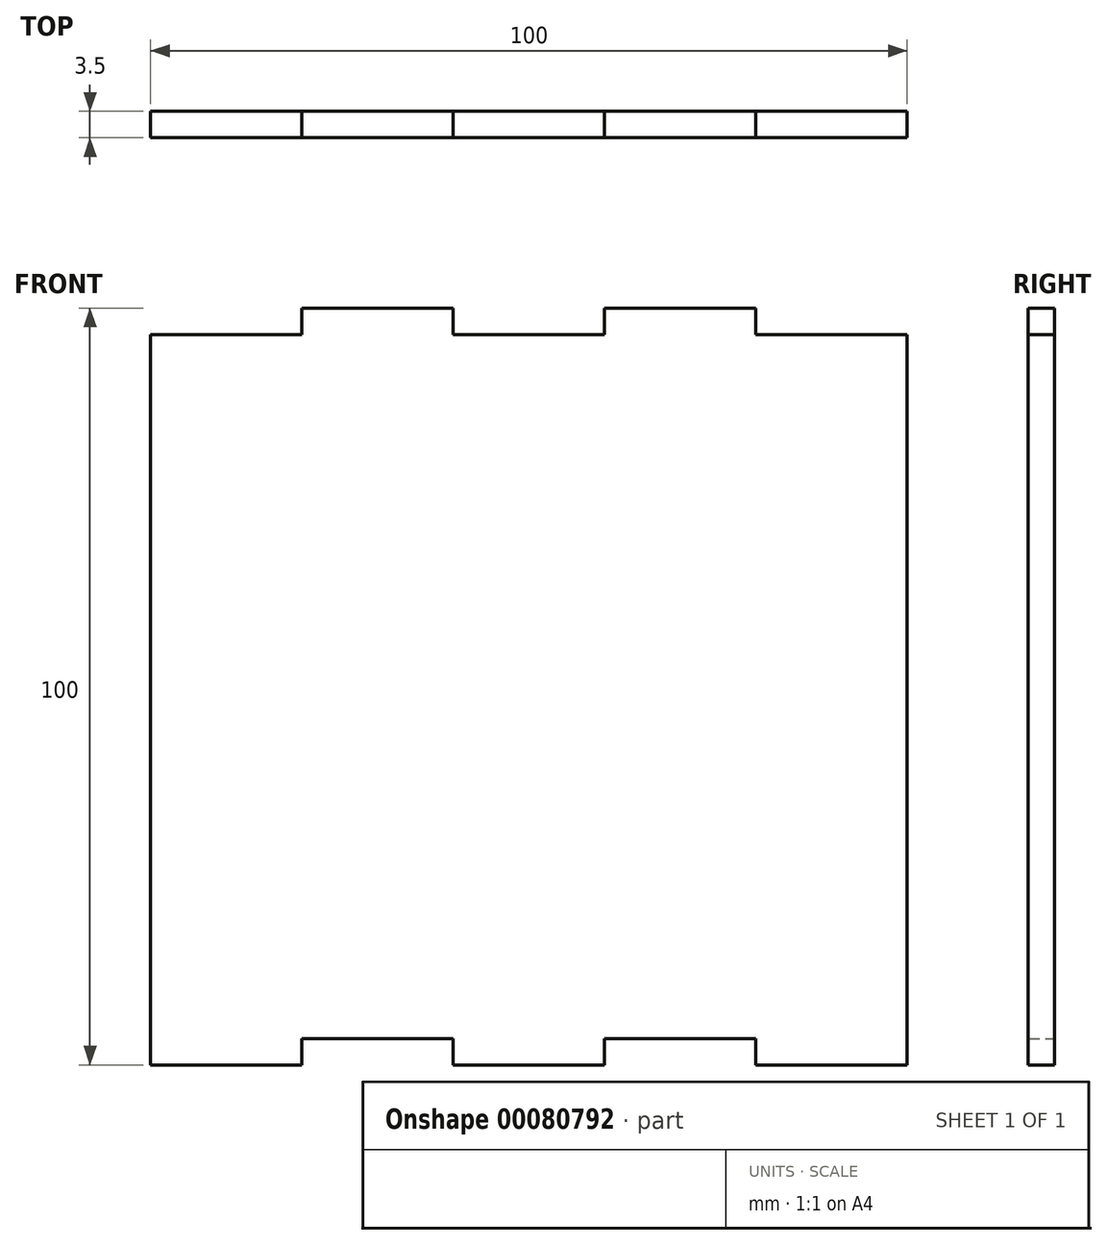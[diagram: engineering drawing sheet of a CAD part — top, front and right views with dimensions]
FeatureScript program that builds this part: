
annotation { "Feature Type Name" : "Feature", "Feature Type Description" : "" }
export const myFeature = defineFeature(function(context is Context, id is Id, definition is map)
    precondition{}
    {
        {
            var Q0;
            Q0=qCreatedBy(makeId("Front.planeOp"),FACE);
            var sketch = newSketch(context, id + "F0", { "sketchPlane" : qUnion([Q0])});
            skLineSegment(sketch, "E0.bottom", {"start": v(-60, 1.92) * mm, "end": v(40, 1.92) * mm});
            skLineSegment(sketch, "E0.top", {"start": v(-60, -98.08) * mm, "end": v(40, -98.08) * mm});
            skLineSegment(sketch, "E0.left", {"start": v(-60, 1.92) * mm, "end": v(-60, -98.08) * mm});
            skLineSegment(sketch, "E0.right", {"start": v(40, 1.92) * mm, "end": v(40, -98.08) * mm});
            skLineSegment(sketch, "E1.direction1", {"start": v(-60, -98.08) * mm, "end": v(-49.65, -98.08) * mm, "construction": true});
            skLineSegment(sketch, "E2", {"start": v(-40, -98.08) * mm, "end": v(-40, -94.58) * mm});
            skLineSegment(sketch, "E3", {"start": v(-40, -94.58) * mm, "end": v(-20, -94.58) * mm});
            skLineSegment(sketch, "E4", {"start": v(-20, -94.58) * mm, "end": v(-20, -98.08) * mm});
            skLineSegment(sketch, "E5", {"start": v(-20, -98.08) * mm, "end": v(0, -98.08) * mm});
            skLineSegment(sketch, "E6", {"start": v(0, -98.08) * mm, "end": v(0, -94.58) * mm});
            skLineSegment(sketch, "E7", {"start": v(-60, -98.08) * mm, "end": v(-40, -98.08) * mm});
            skLineSegment(sketch, "E8", {"start": v(0, -94.58) * mm, "end": v(20, -94.58) * mm});
            skLineSegment(sketch, "E9", {"start": v(20, -94.58) * mm, "end": v(20, -98.08) * mm});
            skLineSegment(sketch, "E10", {"start": v(-60, -1.58) * mm, "end": v(-40, -1.58) * mm});
            skLineSegment(sketch, "E11", {"start": v(-40, -1.58) * mm, "end": v(-40, 1.92) * mm});
            skLineSegment(sketch, "E12", {"start": v(-40, 1.92) * mm, "end": v(-20, 1.92) * mm});
            skLineSegment(sketch, "E13", {"start": v(-20, 1.92) * mm, "end": v(-20, -1.58) * mm});
            skLineSegment(sketch, "E14", {"start": v(-20, -1.58) * mm, "end": v(0, -1.58) * mm});
            skLineSegment(sketch, "E15", {"start": v(0, -1.58) * mm, "end": v(0, 1.92) * mm});
            skLineSegment(sketch, "E16", {"start": v(0, 1.92) * mm, "end": v(20, 1.92) * mm});
            skLineSegment(sketch, "E17", {"start": v(20, 1.92) * mm, "end": v(20, -1.58) * mm});
            skLineSegment(sketch, "E18", {"start": v(20, -1.58) * mm, "end": v(40, -1.58) * mm});
            skSolve(sketch);
        }
        {
            var Q0;
            Q0=makeQuery(id+"F0.imprint","IMPRINT",FACE,{"disambiguationData":[TD([[makeQuery(id+"F0.imprint","IMPRINT",EDGE,{"derivedFrom":sQuery(id+"F0.wireOp",EDGE,"E2")}),1.0]])]});
            extrude(context, id + "F1", {"entities" : qUnion([Q0]), "depth" : 3.5 * mm});
        }
    });
